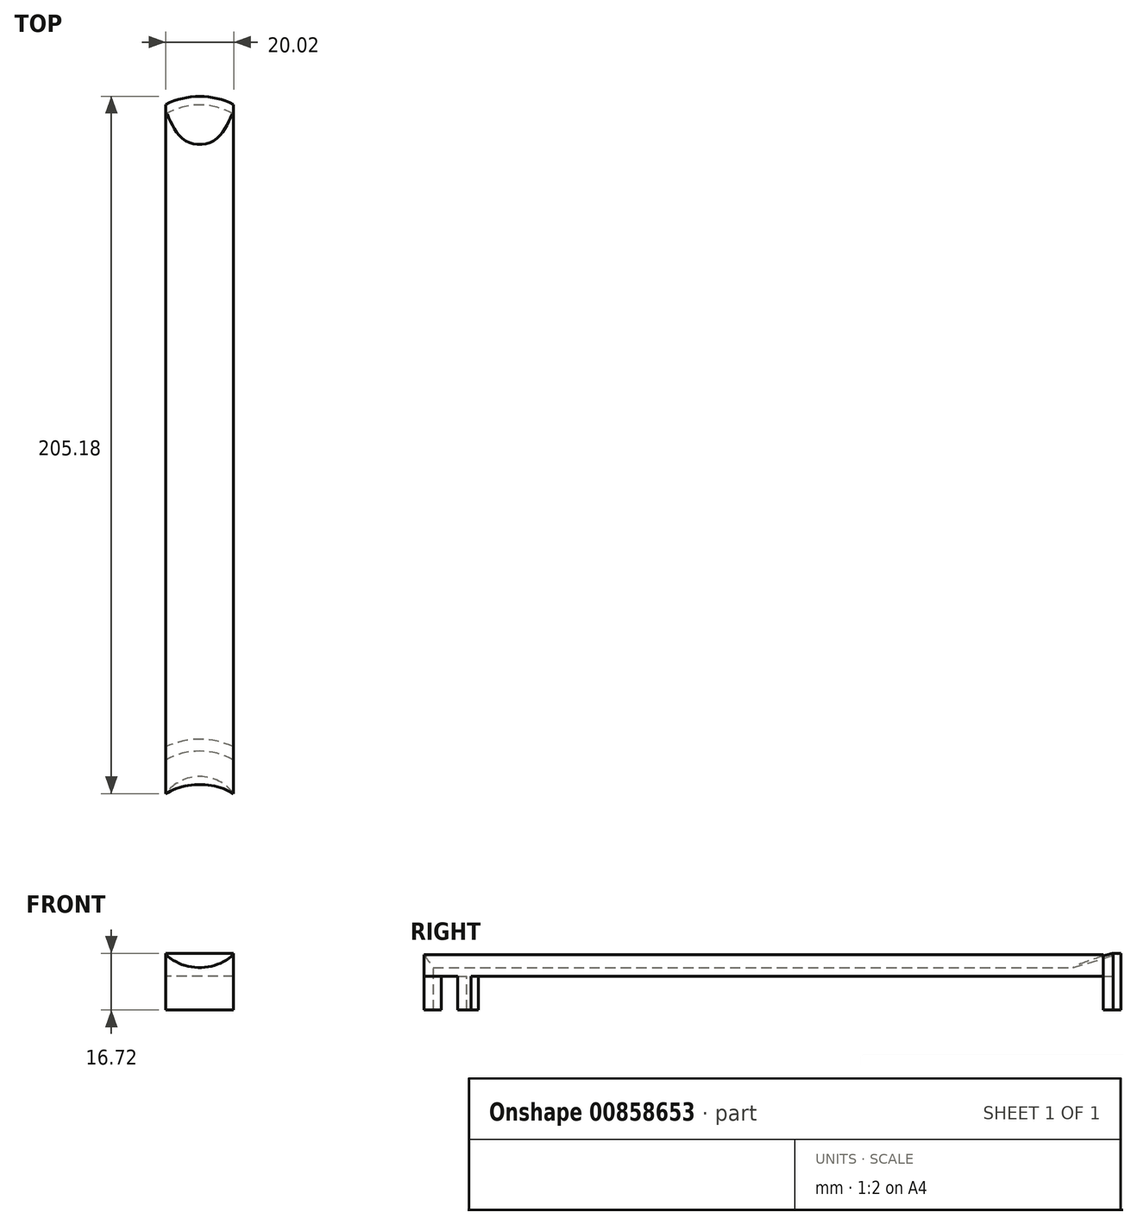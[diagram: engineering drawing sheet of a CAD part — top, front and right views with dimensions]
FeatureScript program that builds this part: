
annotation { "Feature Type Name" : "Feature", "Feature Type Description" : "" }
export const myFeature = defineFeature(function(context is Context, id is Id, definition is map)
    precondition{}
    {
        {
            var Q0;
            Q0=qCreatedBy(makeId("Front.planeOp"),FACE);
            var sketch = newSketch(context, id + "F0", { "sketchPlane" : qUnion([Q0])});
            skLineSegment(sketch, "E0.top", {"start": v(-10, 0) * mm, "end": v(10, 0) * mm});
            skLineSegment(sketch, "E0.left", {"start": v(-10, 6.32) * mm, "end": v(-10, 0) * mm});
            skLineSegment(sketch, "E0.right", {"start": v(10, 6.32) * mm, "end": v(10, 0) * mm});
            skArc(sketch, "E1", {"start": v(-10, 6.32) * mm, "mid": v(0, 2.5) * mm, "end": v(10, 6.32) * mm});
            skSolve(sketch);
        }
        {
            var Q0;
            Q0=makeQuery(id+"F0.imprint","IMPRINT",FACE,{"disambiguationData":[TD([[makeQuery(id+"F0.imprint","IMPRINT",EDGE,{"derivedFrom":sQuery(id+"F0.wireOp",EDGE,"E0.top")}),1.0]])]});
            extrude(context, id + "F1", {"entities" : qUnion([Q0]), "depth" : 100 * mm, "offsetDistance" : 25 * mm, "hasSecondDirection" : true, "secondDirectionOppositeDirection" : true, "secondDirectionDepth" : 100 * mm});
        }
        {
            var Q0;
            Q0=qCreatedBy(makeId("Top.planeOp"),FACE);
            var sketch = newSketch(context, id + "F2", { "sketchPlane" : qUnion([Q0])});
            skArc(sketch, "E2", {"start": v(10, -100) * mm, "mid": v(0, -95) * mm, "end": v(-10, -100) * mm});
            skArc(sketch, "E3", {"start": v(10, -90.18) * mm, "mid": v(0, -87.5) * mm, "end": v(-10, -90.18) * mm});
            skArc(sketch, "E4", {"start": v(4.97, -100) * mm, "mid": v(0, -98.5) * mm, "end": v(-4.97, -100) * mm});
            skArc(sketch, "E5", {"start": v(10, -86.23) * mm, "mid": v(0, -84) * mm, "end": v(-10, -86.23) * mm});
            skLineSegment(sketch, "E6", {"start": v(10, -90.18) * mm, "end": v(10, -86.23) * mm});
            skLineSegment(sketch, "E7", {"start": v(-10, -90.18) * mm, "end": v(-10, -86.23) * mm});
            skLineSegment(sketch, "E8", {"start": v(10, -100) * mm, "end": v(4.97, -100) * mm});
            skLineSegment(sketch, "E9", {"start": v(-4.97, -100) * mm, "end": v(-10, -100) * mm});
            skPoint(sketch, "E10.center.orphan", {"position": v(0, 107.5) * mm});
            skSolve(sketch);
        }
        {
            var Q0;
            Q0 = qSketchRegion(id + "F2", true);
            extrude(context, id + "F3", {"entities" : qUnion([Q0]), "operationType" : NewBodyOperationType.ADD, "oppositeDirection" : true, "depth" : 10 * mm, "offsetDistance" : 25 * mm});
        }
        {
            var Q0;
            Q0=qCreatedBy(makeId("Top.planeOp"),FACE);
            var sketch = newSketch(context, id + "F4", { "sketchPlane" : qUnion([Q0])});
            skCircle(sketch, "E11", {"center": v(0, -117.32) * mm, "radius": 20 * mm});
            skPoint(sketch, "E12.center.orphan", {"position": v(0, 117.32) * mm});
            skSolve(sketch);
        }
        {
            var Q0;
            Q0=makeQuery(id+"F4.imprint","IMPRINT",FACE,{"disambiguationData":[TD([[makeQuery(id+"F4.imprint","IMPRINT",EDGE,{"derivedFrom":sQuery(id+"F4.wireOp",EDGE,"E11")}),1.0]])]});
            extrude(context, id + "F5", {"entities" : qUnion([Q0]), "operationType" : NewBodyOperationType.REMOVE, "oppositeDirection" : true, "depth" : 25 * mm, "offsetDistance" : 25 * mm, "hasSecondDirection" : true, "secondDirectionOppositeDirection" : false, "secondDirectionDepth" : 25 * mm});
        }
        {
            var Q0;
            Q0=qCreatedBy(makeId("Top.planeOp"),FACE);
            var sketch = newSketch(context, id + "F6", { "sketchPlane" : qUnion([Q0])});
            skArc(sketch, "E13", {"start": v(10, 100) * mm, "mid": v(0, 102.68) * mm, "end": v(-10, 100) * mm});
            skLineSegment(sketch, "E14", {"start": v(10, 100) * mm, "end": v(10, 82.68) * mm});
            skLineSegment(sketch, "E15", {"start": v(10, 82.68) * mm, "end": v(-10, 82.68) * mm});
            skLineSegment(sketch, "E16", {"start": v(-10, 82.68) * mm, "end": v(-10, 100) * mm});
            skSolve(sketch);
        }
        {
            var Q0;
            Q0=qCreatedBy(makeId("Right.planeOp"),FACE);
            var sketch = newSketch(context, id + "F7", { "sketchPlane" : qUnion([Q0])});
            skLineSegment(sketch, "E17", {"start": v(82.68, 0) * mm, "end": v(102.7, 5.98) * mm});
            skLineSegment(sketch, "E18", {"start": v(102.7, 5.98) * mm, "end": v(102.7, 0) * mm});
            skLineSegment(sketch, "E19", {"start": v(102.7, 0) * mm, "end": v(82.68, 0) * mm});
            skLineSegment(sketch, "E20", {"start": v(82.68, 0) * mm, "end": v(82.68, 35) * mm, "construction": true});
            skSolve(sketch);
        }
        {
            var Q0;
            Q0=makeQuery(id+"F7.imprint","IMPRINT",FACE,{"disambiguationData":[TD([[makeQuery(id+"F7.imprint","IMPRINT",EDGE,{"derivedFrom":sQuery(id+"F7.wireOp",EDGE,"E17")}),-1.0]])]});
            var Q1;
            Q1=sQuery(id+"F7.wireOp",EDGE,"E20");
            revolve(context, id + "F8", {"operationType" : NewBodyOperationType.ADD, "surfaceOperationType" : NewSurfaceOperationType.NEW, "entities" : qUnion([Q0]), "axis" : qUnion([Q1]), "revolveType" : RevolveType.SYMMETRIC, "angle" : 60 * degree});
        }
        {
            var Q0;
            Q0=makeQuery(id+"F6.imprint","IMPRINT",FACE,{"disambiguationData":[TD([[makeQuery(id+"F6.imprint","IMPRINT",EDGE,{"derivedFrom":sQuery(id+"F6.wireOp",EDGE,"E13")}),1.0]])]});
            var sketch = newSketch(context, id + "F9", { "sketchPlane" : qUnion([Q0])});
            skArc(sketch, "E21", {"start": v(10, 100) * mm, "mid": v(0, 102.68) * mm, "end": v(-10, 100) * mm});
            skArc(sketch, "E22", {"start": v(10, 102.84) * mm, "mid": v(0, 105.18) * mm, "end": v(-10, 102.84) * mm});
            skLineSegment(sketch, "E23", {"start": v(-10, 102.84) * mm, "end": v(-10, 100) * mm});
            skLineSegment(sketch, "E24", {"start": v(10, 102.84) * mm, "end": v(10, 100) * mm});
            skSolve(sketch);
        }
        {
            var Q0;
            Q0=makeQuery(id+"F9.imprint","IMPRINT",FACE,{"disambiguationData":[TD([[makeQuery(id+"F9.imprint","IMPRINT",EDGE,{"derivedFrom":sQuery(id+"F9.wireOp",EDGE,"E21")}),-1.0]])]});
            var Q1;
            Q1=makeQuery(id+"F8.opRevolve","SWEPT_FACE",FACE,{"disambiguationData":[OSD([sQuery(id+"F7.wireOp",EDGE,"E17")])]});
            extrude(context, id + "F10", {"entities" : qUnion([Q0]), "operationType" : NewBodyOperationType.ADD, "endBound" : BoundingType.UP_TO_SURFACE, "depth" : 25 * mm, "endBoundEntityFace" : qUnion([Q1]), "offsetDistance" : 25 * mm, "hasSecondDirection" : true, "secondDirectionOppositeDirection" : true, "secondDirectionDepth" : 10 * mm});
        }
        {
            var Q0;
            {var subQ0=sQuery(id+"F7.wireOp",EDGE,"E19");var subQ1=makeQuery(id+"F8.opRevolve","SWEPT_FACE",FACE,{"disambiguationData":[OSD([subQ0])]});var subQ2=sQuery(id+"F7.wireOp",EDGE,"E18");var subQ3=sQuery(id+"F7.wireOp",EDGE,"E17");var subQ4=makeQuery(id+"F3.opExtrude","SWEPT_FACE",FACE,{"disambiguationData":[OSD([sQuery(id+"F2.wireOp",EDGE,"E6")])]});var subQ5=makeQuery(id+"F3.opExtrude","SWEPT_FACE",FACE,{"disambiguationData":[OSD([sQuery(id+"F2.wireOp",EDGE,"E7")])]});var subQ6=sQuery(id+"F0.wireOp",EDGE,"E0.top");var subQ7=makeQuery(id+"F1.opExtrude","SWEPT_FACE",FACE,{"disambiguationData":[OSD([subQ6])]});var subQ8=makeQuery(id+"F3.opExtrude","SWEPT_FACE",FACE,{"disambiguationData":[OSD([sQuery(id+"F2.wireOp",EDGE,"E5")])]});var subQ9=sQuery(id+"F0.wireOp",EDGE,"E0.left");var subQ10=makeQuery(id+"F1.opExtrude","SWEPT_FACE",FACE,{"disambiguationData":[OSD([subQ9])]});var subQ11=sQuery(id+"F0.wireOp",EDGE,"E0.right");var subQ12=makeQuery(id+"F1.opExtrude","SWEPT_FACE",FACE,{"disambiguationData":[OSD([subQ11])]});Q0=makeQuery(id+"F10.boolean.opBoolean","SPLIT",FACE,{"disambiguationData":[TD([subQ7,subQ10,subQ12,subQ8,subQ4,subQ5,makeQuery(id+"F8.opRevolve","CAP_FACE",FACE,{"disambiguationData":[OSD([subQ3,subQ2,subQ0])],"isStart":true}),makeQuery(id+"F8.opRevolve","CAP_FACE",FACE,{"disambiguationData":[OSD([subQ3,subQ2,subQ0])],"isStart":false}),subQ1,makeQuery(id+"F10.opExtrude","SWEPT_FACE",FACE,{"disambiguationData":[OSD([sQuery(id+"F9.wireOp",EDGE,"E21")])]}),makeQuery(id+"F10.opExtrude","SWEPT_FACE",FACE,{"disambiguationData":[OSD([sQuery(id+"F9.wireOp",EDGE,"E23")])]}),makeQuery(id+"F10.opExtrude","SWEPT_FACE",FACE,{"disambiguationData":[OSD([sQuery(id+"F9.wireOp",EDGE,"E24")])]})])],"derivedFrom":makeQuery(id+"F8.boolean.opBoolean","MERGE",FACE,{"derivedFrom":[makeQuery(id+"F3.boolean.opBoolean","SPLIT",FACE,{"disambiguationData":[TD([subQ8])],"derivedFrom":subQ7}),subQ1]})});}
            var sketch = newSketch(context, id + "F11", { "sketchPlane" : qUnion([Q0])});
            skArc(sketch, "E25", {"start": v(-10, -90.18) * mm, "mid": v(0, -95.18) * mm, "end": v(10, -90.18) * mm});
            skArc(sketch, "E26", {"start": v(-10, -90.18) * mm, "mid": v(0, -93.21) * mm, "end": v(10, -90.18) * mm});
            skSolve(sketch);
        }
        {
            var Q0;
            Q0=sQuery(id+"F11.wireOp",EDGE,"E25");
            var Q1;
            Q1=sQuery(id+"F11.wireOp",EDGE,"E26");
            extrude(context, id + "F12", {"bodyType" : ToolBodyType.SURFACE, "surfaceEntities" : qUnion([Q0, Q1]), "depth" : 10 * mm, "offsetDistance" : 25 * mm});
        }
    });
